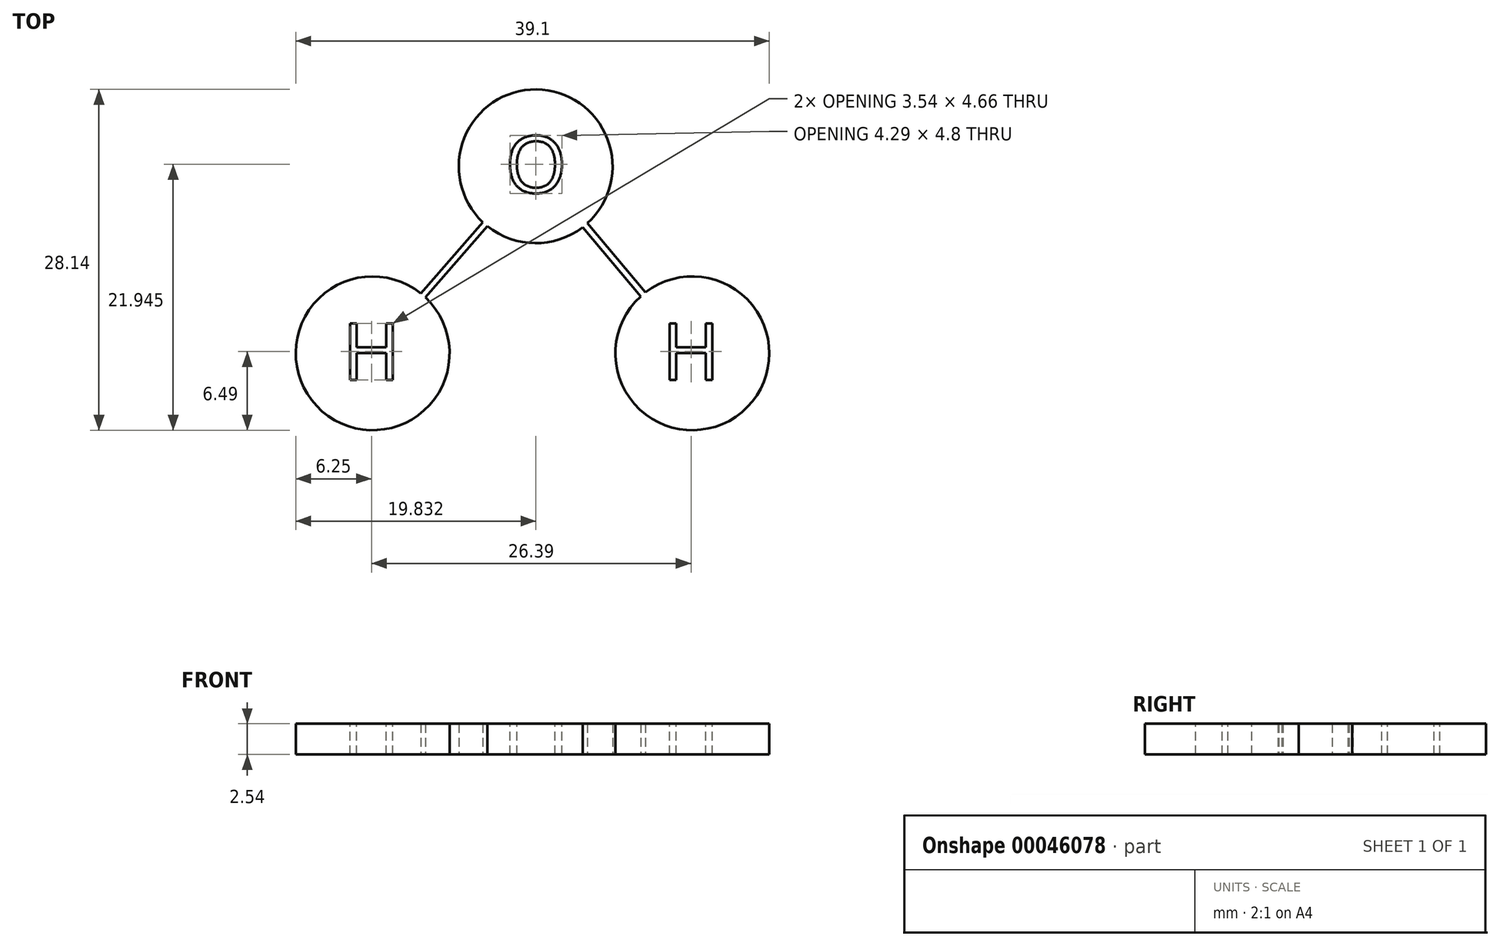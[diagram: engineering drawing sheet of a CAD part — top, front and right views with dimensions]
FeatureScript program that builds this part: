
annotation { "Feature Type Name" : "Feature", "Feature Type Description" : "" }
export const myFeature = defineFeature(function(context is Context, id is Id, definition is map)
    precondition{}
    {
        {
            var Q0;
            Q0=qCreatedBy(makeId("Top.planeOp"),FACE);
            var sketch = newSketch(context, id + "F0", { "sketchPlane" : qUnion([Q0])});
            skArc(sketch, "E0", {"start": v(-1.22, 2.15) * mm, "mid": v(2.7, 0.75) * mm, "end": v(6.64, 2.07) * mm});
            skArc(sketch, "E1", {"start": v(-6.72, -3.4) * mm, "mid": v(-14.87, -13.13) * mm, "end": v(-6.34, -3.73) * mm});
            skArc(sketch, "E2", {"start": v(11.43, -3.64) * mm, "mid": v(19.78, -13.21) * mm, "end": v(11.82, -3.32) * mm});
            skPoint(sketch, "E3.end.orphan", {"position": v(-2.35, 3.32) * mm});
            skPoint(sketch, "E3.start.orphan", {"position": v(-7.9, -2.65) * mm});
            skPoint(sketch, "E4.start.orphan", {"position": v(0.92, 1.02) * mm});
            skPoint(sketch, "E5.start.orphan", {"position": v(4.6, 1.02) * mm});
            skPoint(sketch, "E6.end.orphan", {"position": v(12.9, -2.65) * mm});
            skPoint(sketch, "E6.start.orphan", {"position": v(7.86, 3.32) * mm});
            skLineSegment(sketch, "E7.0", {"start": v(-6.34, -3.72) * mm, "end": v(-1.22, 2.14) * mm});
            skLineSegment(sketch, "E8.0", {"start": v(-6.72, -3.4) * mm, "end": v(-1.6, 2.48) * mm});
            skLineSegment(sketch, "E9.0", {"start": v(7.03, 2.4) * mm, "end": v(11.82, -3.32) * mm});
            skLineSegment(sketch, "E10.0", {"start": v(6.64, 2.07) * mm, "end": v(11.43, -3.64) * mm});
            skLineSegment(sketch, "E11", {"start": v(-1.22, 2.14) * mm, "end": v(-1.22, 2.15) * mm});
            skLineSegment(sketch, "E12", {"start": v(-1.6, 2.48) * mm, "end": v(-1.6, 2.48) * mm});
            skLineSegment(sketch, "E13", {"start": v(-6.72, -3.4) * mm, "end": v(-6.72, -3.4) * mm});
            skLineSegment(sketch, "E14", {"start": v(-6.34, -3.72) * mm, "end": v(-6.34, -3.73) * mm});
            skArc(sketch, "E15.trimOffspring", {"start": v(7.03, 2.4) * mm, "mid": v(2.82, 13.45) * mm, "end": v(-1.6, 2.48) * mm});
            skSolve(sketch);
        }
        {
            var Q0;
            Q0=makeQuery(id+"F0.imprint","IMPRINT",FACE,{"disambiguationData":[TD([[makeQuery(id+"F0.imprint","IMPRINT",EDGE,{"derivedFrom":sQuery(id+"F0.wireOp",EDGE,"E0")}),1.0]])]});
            extrude(context, id + "F1", {"entities" : qUnion([Q0]), "depth" : 2.54 * mm});
        }
        {
            var Q0;
            Q0=makeQuery(id+"F1.opExtrude","CAP_FACE",FACE,{"disambiguationData":[OSD([sQuery(id+"F0.wireOp",EDGE,"E0"),sQuery(id+"F0.wireOp",EDGE,"E1"),sQuery(id+"F0.wireOp",EDGE,"E2"),sQuery(id+"F0.wireOp",EDGE,"E7.0"),sQuery(id+"F0.wireOp",EDGE,"E8.0"),sQuery(id+"F0.wireOp",EDGE,"E9.0"),sQuery(id+"F0.wireOp",EDGE,"E10.0"),sQuery(id+"F0.wireOp",EDGE,"E11"),sQuery(id+"F0.wireOp",EDGE,"E12"),sQuery(id+"F0.wireOp",EDGE,"E13"),sQuery(id+"F0.wireOp",EDGE,"E14"),sQuery(id+"F0.wireOp",EDGE,"E15.trimOffspring")])],"isStart":false});
            var sketch = newSketch(context, id + "F2", { "sketchPlane" : qUnion([Q0])});
            skText(sketch, "E16", { "text": "H", "fontName": "OpenSans-Regular.ttf"});
            skText(sketch, "E17", { "text": "H", "fontName": "OpenSans-Regular.ttf"});
            skText(sketch, "E18", { "text": "O", "fontName": "OpenSans-Regular.ttf"});
            const initialGuessF2  = {"E16": [-0.01321, -0.01053, 1, 0, 0.0047], "E17": [0.01318, -0.01053, 1, 0, 0.0047], "E18": [0.00024, 0.00492, 1, 0, 0.0047]};
            skSetInitialGuess(sketch, initialGuessF2);
            skSolve(sketch);
        }
        {
            var Q0;
            Q0 = qSketchRegion(id + "F2", true);
            extrude(context, id + "F3", {"entities" : qUnion([Q0]), "operationType" : NewBodyOperationType.REMOVE, "oppositeDirection" : true, "depth" : 25.4 * mm});
        }
    });
